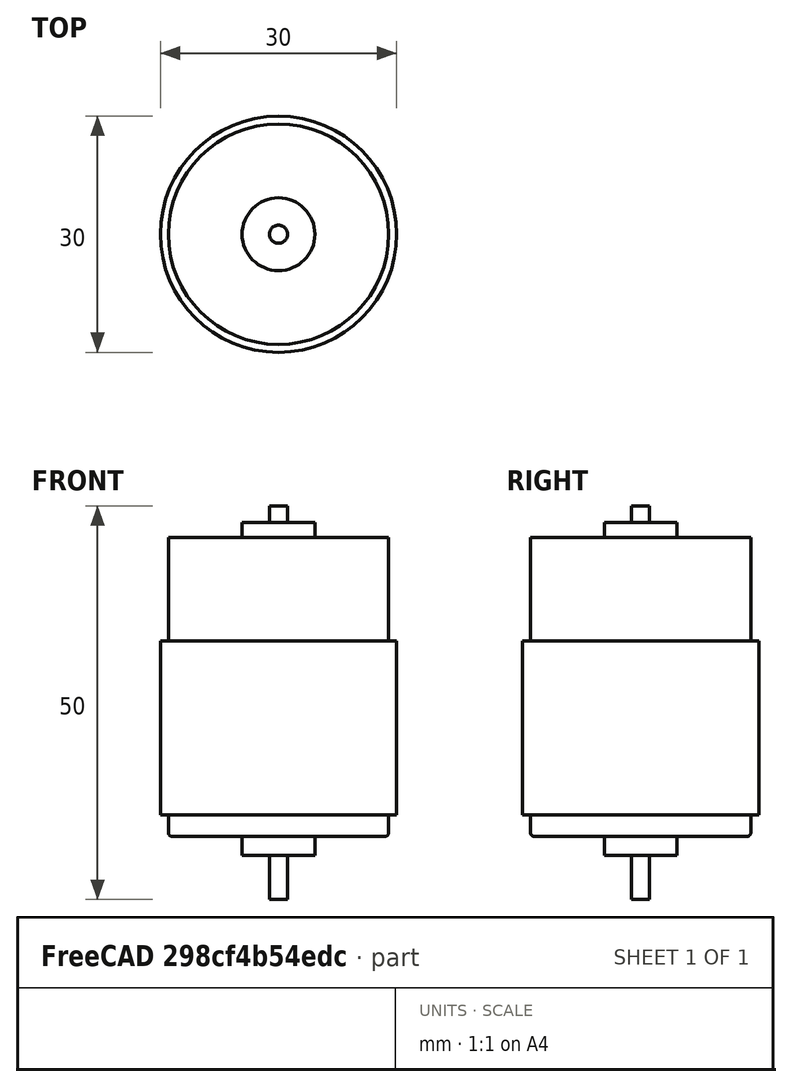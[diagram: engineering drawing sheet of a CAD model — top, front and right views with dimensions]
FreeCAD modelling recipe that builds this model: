
FCSTD DOCUMENT  (FreeCAD 0.15R4671 (Git))
Label: Motor-CC-12V-MITSUMI
License: All rights reserved
LicenseURL: http://es.wikipedia.org/wiki/Todos_los_derechos_reservados
objects: Part::Cylinder×4, Part::MultiFuse×2, Part::Fillet×1
note: 7 computed .brp shape members not serialized (recipe doc carries the construction recipe); baked Part::Feature solids carry a one-line shape summary decoded from their .brp

FEATURE [Part::Cylinder] Cylinder  label="Cilindro003"
  Angle = 360
  Height = 22.1
  Placement = pos=(0,0,2.7) rot=(0,0,1;0rad)
  Radius = 15
FEATURE [Part::Cylinder] Cylinder001  label="Cilindro004"
  Angle = 360
  Height = 38
  Radius = 14
FEATURE [Part::Fillet] Fillet
  Base = -> Cylinder001
  Edges = 1 edges r=0.5: [Edge3]
FEATURE [Part::Cylinder] Cylinder002  label="Cilindro005"
  Angle = 360
  Height = 42.3
  Placement = pos=(0,0,-2.4) rot=(0,0,1;0rad)
  Radius = 4.625
FEATURE [Part::Cylinder] Cylinder003  label="Cilindro006"
  Angle = 360
  Height = 50
  Placement = pos=(0,0,-8) rot=(0,0,1;0rad)
  Radius = 1.15
FEATURE [Part::MultiFuse] Fusion
  Shapes = -> [Cylinder,Fillet,Cylinder002]
FEATURE [Part::MultiFuse] Fusion001  label="motor"
  Shapes = -> [Cylinder003,Fusion]
